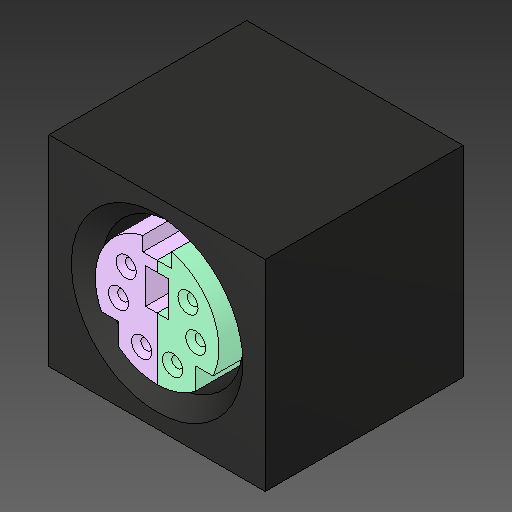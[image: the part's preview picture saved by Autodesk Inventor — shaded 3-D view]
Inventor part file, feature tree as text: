
AUTODESK INVENTOR PART (.ipt)
format: ipt  version: 2018.2 (Build 222227000, 227)  size: 148,992 bytes
history: native  units: mm
features: other x5, chamfer x1
ambient origin geometry x8: Origin, YZ Plane, XZ Plane, XY Plane, X Axis, Y Axis, Z Axis, Center Point
bodies: Body1 (feature_tree), Body2 (feature_tree), Body3 (feature_tree)
feature tree (6):
  other  "ソリッド1"
  other  "ソリッド2"
  other  "ソリッド3"
  chamfer  "Chamfer2"  [1 undecoded]
  other  "Split1[1]"
  other  "Split1[2]"
note: 1 required parameter value undecoded (feature->parameter linkage not recoverable at this tier; creation-order binding heuristic only, values carry confidence <= 0.55)
